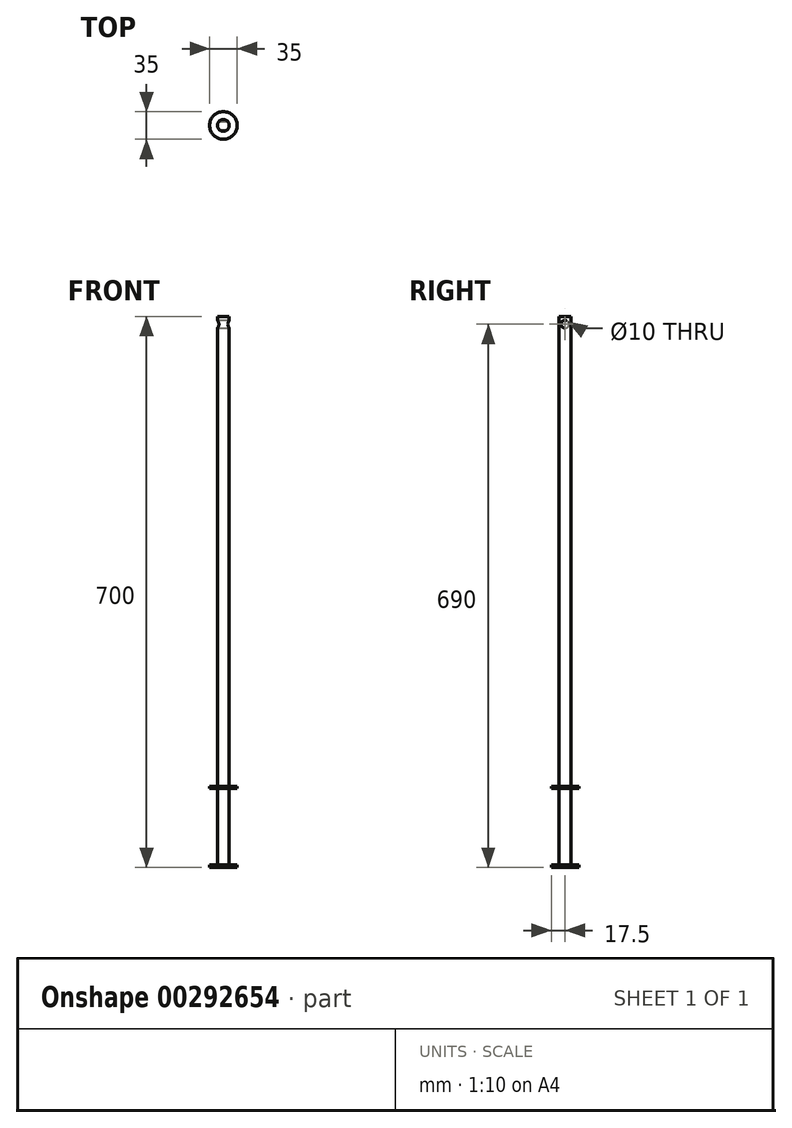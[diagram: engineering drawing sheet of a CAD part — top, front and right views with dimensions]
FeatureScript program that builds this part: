
annotation { "Feature Type Name" : "Feature", "Feature Type Description" : "" }
export const myFeature = defineFeature(function(context is Context, id is Id, definition is map)
    precondition{}
    {
        {
            var Q0;
            Q0=qCreatedBy(makeId("Top.planeOp"),FACE);
            var sketch = newSketch(context, id + "F0", { "sketchPlane" : qUnion([Q0])});
            skCircle(sketch, "E0", {"center": v(0, 0) * mm, "radius": 7.5 * mm});
            skSolve(sketch);
        }
        {
            var Q0;
            Q0 = qSketchRegion(id + "F0", true);
            extrude(context, id + "F1", {"entities" : qUnion([Q0]), "depth" : 700 * mm});
        }
        {
            var Q0;
            Q0=qCreatedBy(makeId("Right.planeOp"),FACE);
            var sketch = newSketch(context, id + "F2", { "sketchPlane" : qUnion([Q0])});
            skCircle(sketch, "E1", {"center": v(0, 690) * mm, "radius": 5 * mm});
            skSolve(sketch);
        }
        {
            var Q0;
            Q0 = qSketchRegion(id + "F2", true);
            extrude(context, id + "F3", {"entities" : qUnion([Q0]), "operationType" : NewBodyOperationType.REMOVE, "endBound" : BoundingType.THROUGH_ALL, "oppositeDirection" : true, "depth" : 25 * mm, "hasSecondDirection" : true, "secondDirectionBound" : SecondDirectionBoundingType.THROUGH_ALL, "secondDirectionOppositeDirection" : false, "secondDirectionDepth" : 25 * mm});
        }
        {
            var Q0;
            Q0=qCreatedBy(makeId("Top.planeOp"),FACE);
            cPlane(context, id + "F4", {"entities" : qUnion([Q0]), "cplaneType" : CPlaneType.OFFSET, "offset" : 100 * mm, "width" : 150 * mm, "height" : 150 * mm});
        }
        {
            var Q0;
            Q0=qCreatedBy(makeId("Top.planeOp"),FACE);
            var sketch = newSketch(context, id + "F5", { "sketchPlane" : qUnion([Q0])});
            skCircle(sketch, "E2", {"center": v(0, 0) * mm, "radius": 17.5 * mm});
            skSolve(sketch);
        }
        {
            var Q0;
            Q0 = qSketchRegion(id + "F5", true);
            extrude(context, id + "F6", {"entities" : qUnion([Q0]), "operationType" : NewBodyOperationType.ADD, "depth" : 3 * mm});
        }
        {
            var Q0;
            Q0=qCreatedBy(id+"F4.planeOp",FACE);
            var sketch = newSketch(context, id + "F7", { "sketchPlane" : qUnion([Q0])});
            skCircle(sketch, "E3", {"center": v(0, 0) * mm, "radius": 17.5 * mm});
            skSolve(sketch);
        }
        {
            var Q0;
            Q0 = qSketchRegion(id + "F7", true);
            extrude(context, id + "F8", {"entities" : qUnion([Q0]), "operationType" : NewBodyOperationType.ADD, "depth" : 3 * mm});
        }
    });
